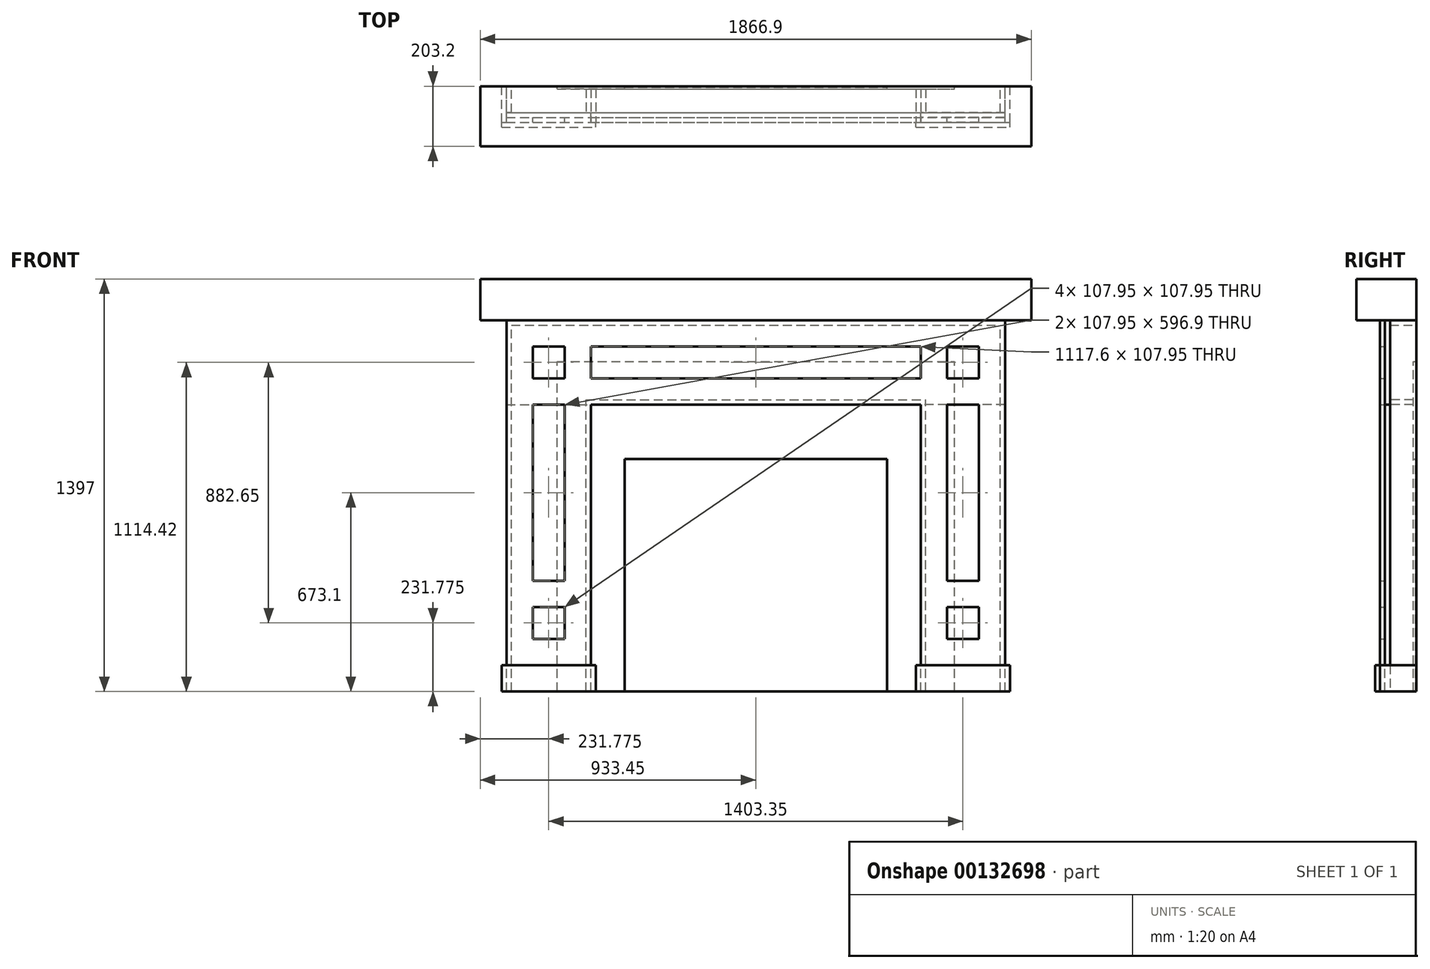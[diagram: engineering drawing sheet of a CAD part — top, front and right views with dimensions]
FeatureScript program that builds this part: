
annotation { "Feature Type Name" : "Feature", "Feature Type Description" : "" }
export const myFeature = defineFeature(function(context is Context, id is Id, definition is map)
    precondition{}
    {
        {
            var Q0;
            Q0=qCreatedBy(makeId("Front.planeOp"),FACE);
            var sketch = newSketch(context, id + "F0", { "sketchPlane" : qUnion([Q0])});
            skLineSegment(sketch, "E0.bottom", {"start": v(0, 0) * mm, "end": v(889, 0) * mm});
            skLineSegment(sketch, "E0.top", {"start": v(0, 787.4) * mm, "end": v(889, 787.4) * mm});
            skLineSegment(sketch, "E0.left", {"start": v(0, 0) * mm, "end": v(0, 787.4) * mm});
            skLineSegment(sketch, "E0.right", {"start": v(889, 0) * mm, "end": v(889, 787.4) * mm});
            skSolve(sketch);
        }
        {
            var Q0;
            Q0=makeQuery(id+"F0.imprint","IMPRINT",FACE,{"disambiguationData":[TD([[makeQuery(id+"F0.imprint","IMPRINT",EDGE,{"derivedFrom":sQuery(id+"F0.wireOp",EDGE,"E0.bottom")}),1.0]])]});
            extrude(context, id + "F1", {"entities" : qUnion([Q0]), "depth" : 2.54 * mm});
        }
        {
            var Q0;
            Q0=qCreatedBy(makeId("Front.planeOp"),FACE);
            var sketch = newSketch(context, id + "F2", { "sketchPlane" : qUnion([Q0])});
            skLineSegment(sketch, "E1.bottom", {"start": v(0, 0) * mm, "end": v(-228.6, 0) * mm});
            skLineSegment(sketch, "E1.left", {"start": v(0, 0) * mm, "end": v(0, 787.4) * mm});
            skLineSegment(sketch, "E2", {"start": v(0, 787.4) * mm, "end": v(889, 787.4) * mm});
            skLineSegment(sketch, "E3.0", {"start": v(889, 0) * mm, "end": v(889, 787.4) * mm});
            skLineSegment(sketch, "E4", {"start": v(889, 0) * mm, "end": v(1117.6, 0) * mm});
            skLineSegment(sketch, "E5", {"start": v(1117.6, 0) * mm, "end": v(1117.6, 1117.6) * mm});
            skLineSegment(sketch, "E6", {"start": v(-228.6, 0) * mm, "end": v(-228.6, 1117.6) * mm});
            skLineSegment(sketch, "E7", {"start": v(-228.6, 1117.6) * mm, "end": v(1117.6, 1117.6) * mm});
            skSolve(sketch);
        }
        {
            var Q0;
            Q0 = qSketchRegion(id + "F2", true);
            extrude(context, id + "F3", {"entities" : qUnion([Q0]), "operationType" : NewBodyOperationType.ADD, "depth" : 9.52 * mm});
        }
        {
            var Q0;
            Q0=qCreatedBy(makeId("Front.planeOp"),FACE);
            var sketch = newSketch(context, id + "F4", { "sketchPlane" : qUnion([Q0])});
            skLineSegment(sketch, "E8.bottom", {"start": v(1272.39, 0) * mm, "end": v(1289.05, 0) * mm});
            skLineSegment(sketch, "E8.top", {"start": v(1272.39, 1240.64) * mm, "end": v(1289.05, 1240.64) * mm});
            skLineSegment(sketch, "E8.left", {"start": v(1272.39, 0) * mm, "end": v(1272.39, 1240.64) * mm});
            skLineSegment(sketch, "E8.right", {"start": v(1289.05, 0) * mm, "end": v(1289.05, 1240.64) * mm});
            skLineSegment(sketch, "E9.bottom", {"start": v(-400.05, 1257.3) * mm, "end": v(1289.05, 1257.3) * mm});
            skLineSegment(sketch, "E9.top", {"start": v(-400.05, 1240.64) * mm, "end": v(1289.05, 1240.64) * mm});
            skLineSegment(sketch, "E9.left", {"start": v(-400.05, 1257.3) * mm, "end": v(-400.05, 1240.64) * mm});
            skLineSegment(sketch, "E9.right", {"start": v(1289.05, 1257.3) * mm, "end": v(1289.05, 1240.64) * mm});
            skLineSegment(sketch, "E10.bottom", {"start": v(-383.39, 0) * mm, "end": v(-400.05, 0) * mm});
            skLineSegment(sketch, "E10.top", {"start": v(-383.39, 1240.64) * mm, "end": v(-400.05, 1240.64) * mm});
            skLineSegment(sketch, "E10.left", {"start": v(-383.39, 0) * mm, "end": v(-383.39, 1240.64) * mm});
            skLineSegment(sketch, "E10.right", {"start": v(-400.05, 0) * mm, "end": v(-400.05, 1240.64) * mm});
            skSolve(sketch);
        }
        {
            var Q0;
            Q0=makeQuery(id+"F4.imprint","IMPRINT",FACE,{"disambiguationData":[TD([[makeQuery(id+"F4.imprint","IMPRINT",EDGE,{"derivedFrom":sQuery(id+"F4.wireOp",EDGE,"E10.bottom")}),-1.0]])]});
            var Q1;
            Q1=makeQuery(id+"F4.imprint","IMPRINT",FACE,{"disambiguationData":[TD([[makeQuery(id+"F4.imprint","IMPRINT",EDGE,{"derivedFrom":sQuery(id+"F4.wireOp",EDGE,"E9.bottom")}),-1.0]])]});
            var Q2;
            Q2=makeQuery(id+"F4.imprint","IMPRINT",FACE,{"disambiguationData":[TD([[makeQuery(id+"F4.imprint","IMPRINT",EDGE,{"derivedFrom":sQuery(id+"F4.wireOp",EDGE,"E8.bottom")}),1.0]])]});
            extrude(context, id + "F5", {"entities" : qUnion([Q0, Q1, Q2]), "depth" : 88.9 * mm});
        }
        {
            var Q0;
            Q0=makeQuery(id+"F5.opExtrude","CAP_FACE",FACE,{"disambiguationData":[OSD([sQuery(id+"F4.wireOp",EDGE,"E9.bottom"),sQuery(id+"F4.wireOp",EDGE,"E9.top"),sQuery(id+"F4.wireOp",EDGE,"E9.left"),sQuery(id+"F4.wireOp",EDGE,"E9.right")])],"isStart":false});
            var sketch = newSketch(context, id + "F6", { "sketchPlane" : qUnion([Q0])});
            skLineSegment(sketch, "E11.bottom", {"start": v(-400.05, 1257.3) * mm, "end": v(1289.05, 1257.3) * mm});
            skLineSegment(sketch, "E11.top", {"start": v(-400.05, 971.55) * mm, "end": v(1289.05, 971.55) * mm});
            skLineSegment(sketch, "E11.left", {"start": v(-400.05, 1257.3) * mm, "end": v(-400.05, 971.55) * mm});
            skLineSegment(sketch, "E11.right", {"start": v(1289.05, 1257.3) * mm, "end": v(1289.05, 971.55) * mm});
            skSolve(sketch);
        }
        {
            var Q0;
            Q0 = qSketchRegion(id + "F6", true);
            extrude(context, id + "F7", {"entities" : qUnion([Q0]), "depth" : 16.66 * mm});
        }
        {
            var Q0;
            Q0=makeQuery(id+"F5.opExtrude","CAP_FACE",FACE,{"disambiguationData":[OSD([sQuery(id+"F4.wireOp",EDGE,"E10.bottom"),sQuery(id+"F4.wireOp",EDGE,"E10.top"),sQuery(id+"F4.wireOp",EDGE,"E10.left"),sQuery(id+"F4.wireOp",EDGE,"E10.right")])],"isStart":false});
            var sketch = newSketch(context, id + "F8", { "sketchPlane" : qUnion([Q0])});
            skLineSegment(sketch, "E12.bottom", {"start": v(-400.05, 0) * mm, "end": v(-114.3, 0) * mm});
            skLineSegment(sketch, "E12.top", {"start": v(-400.05, 971.55) * mm, "end": v(-114.3, 971.55) * mm});
            skLineSegment(sketch, "E12.left", {"start": v(-400.05, 0) * mm, "end": v(-400.05, 971.55) * mm});
            skLineSegment(sketch, "E12.right", {"start": v(-114.3, 0) * mm, "end": v(-114.3, 971.55) * mm});
            skLineSegment(sketch, "E13.0", {"start": v(1289.05, 0) * mm, "end": v(1289.05, 971.55) * mm});
            skLineSegment(sketch, "E14.bottom", {"start": v(1289.05, 0) * mm, "end": v(1003.3, 0) * mm});
            skLineSegment(sketch, "E14.top", {"start": v(1289.05, 971.55) * mm, "end": v(1003.3, 971.55) * mm});
            skLineSegment(sketch, "E14.right", {"start": v(1003.3, 0) * mm, "end": v(1003.3, 971.55) * mm});
            skPoint(sketch, "E15.orphan", {"position": v(1289.05, 0) * mm});
            skSolve(sketch);
        }
        {
            var Q0;
            Q0 = qSketchRegion(id + "F8", true);
            extrude(context, id + "F9", {"entities" : qUnion([Q0]), "depth" : 16.66 * mm});
        }
        {
            var Q0;
            Q0=makeQuery(id+"F9.opExtrude","CAP_FACE",FACE,{"disambiguationData":[OSD([sQuery(id+"F8.wireOp",EDGE,"E12.bottom"),sQuery(id+"F8.wireOp",EDGE,"E12.top"),sQuery(id+"F8.wireOp",EDGE,"E12.left"),sQuery(id+"F8.wireOp",EDGE,"E12.right")])],"isStart":false});
            var sketch = newSketch(context, id + "F10", { "sketchPlane" : qUnion([Q0])});
            skLineSegment(sketch, "E16.0", {"start": v(-400.05, 0) * mm, "end": v(-400.05, 971.55) * mm});
            skLineSegment(sketch, "E17.0", {"start": v(-400.05, 1257.3) * mm, "end": v(-400.05, 971.55) * mm});
            skLineSegment(sketch, "E18.0", {"start": v(-400.05, 1257.3) * mm, "end": v(1289.05, 1257.3) * mm});
            skLineSegment(sketch, "E19.0", {"start": v(1289.05, 1257.3) * mm, "end": v(1289.05, 971.55) * mm});
            skLineSegment(sketch, "E20.0", {"start": v(1289.05, 0) * mm, "end": v(1289.05, 971.55) * mm});
            skLineSegment(sketch, "E21.0", {"start": v(1289.05, 0) * mm, "end": v(1003.3, 0) * mm});
            skLineSegment(sketch, "E22.0", {"start": v(1003.3, 0) * mm, "end": v(1003.3, 971.55) * mm});
            skLineSegment(sketch, "E23.0", {"start": v(-114.3, 971.55) * mm, "end": v(1003.3, 971.55) * mm});
            skLineSegment(sketch, "E24.0", {"start": v(-114.3, 0) * mm, "end": v(-114.3, 971.55) * mm});
            skLineSegment(sketch, "E25", {"start": v(-400.05, 0) * mm, "end": v(-114.3, 0) * mm});
            skLineSegment(sketch, "E26.bottom", {"start": v(-311.15, 177.8) * mm, "end": v(-203.2, 177.8) * mm});
            skLineSegment(sketch, "E26.top", {"start": v(-311.15, 285.75) * mm, "end": v(-203.2, 285.75) * mm});
            skLineSegment(sketch, "E26.left", {"start": v(-311.15, 177.8) * mm, "end": v(-311.15, 285.75) * mm});
            skLineSegment(sketch, "E26.right", {"start": v(-203.2, 177.8) * mm, "end": v(-203.2, 285.75) * mm});
            skLineSegment(sketch, "E27.bottom", {"start": v(-311.15, 1168.4) * mm, "end": v(-203.2, 1168.4) * mm});
            skLineSegment(sketch, "E27.top", {"start": v(-311.15, 1060.45) * mm, "end": v(-203.2, 1060.45) * mm});
            skLineSegment(sketch, "E27.left", {"start": v(-311.15, 1168.4) * mm, "end": v(-311.15, 1060.45) * mm});
            skLineSegment(sketch, "E27.right", {"start": v(-203.2, 1168.4) * mm, "end": v(-203.2, 1060.45) * mm});
            skPoint(sketch, "E28.oppositeSnap0", {"position": v(-203.2, 231.77) * mm});
            skLineSegment(sketch, "E28.bottom", {"start": v(-311.15, 374.65) * mm, "end": v(-203.2, 374.65) * mm});
            skLineSegment(sketch, "E28.top", {"start": v(-311.15, 971.55) * mm, "end": v(-203.2, 971.55) * mm});
            skLineSegment(sketch, "E28.left", {"start": v(-311.15, 374.65) * mm, "end": v(-311.15, 971.55) * mm});
            skLineSegment(sketch, "E28.right", {"start": v(-203.2, 374.65) * mm, "end": v(-203.2, 971.55) * mm});
            skLineSegment(sketch, "E29.bottom", {"start": v(-114.3, 1168.4) * mm, "end": v(1003.3, 1168.4) * mm});
            skLineSegment(sketch, "E29.top", {"start": v(-114.3, 1060.45) * mm, "end": v(1003.3, 1060.45) * mm});
            skLineSegment(sketch, "E29.left", {"start": v(-114.3, 1168.4) * mm, "end": v(-114.3, 1060.45) * mm});
            skLineSegment(sketch, "E29.right", {"start": v(1003.3, 1168.4) * mm, "end": v(1003.3, 1060.45) * mm});
            skLineSegment(sketch, "E30.bottom", {"start": v(1200.15, 1168.4) * mm, "end": v(1092.2, 1168.4) * mm});
            skLineSegment(sketch, "E30.top", {"start": v(1200.15, 1060.45) * mm, "end": v(1092.2, 1060.45) * mm});
            skLineSegment(sketch, "E30.left", {"start": v(1200.15, 1168.4) * mm, "end": v(1200.15, 1060.45) * mm});
            skLineSegment(sketch, "E30.right", {"start": v(1092.2, 1168.4) * mm, "end": v(1092.2, 1060.45) * mm});
            skLineSegment(sketch, "E31.bottom", {"start": v(1200.15, 177.8) * mm, "end": v(1092.2, 177.8) * mm});
            skLineSegment(sketch, "E31.top", {"start": v(1200.15, 285.75) * mm, "end": v(1092.2, 285.75) * mm});
            skLineSegment(sketch, "E31.left", {"start": v(1200.15, 177.8) * mm, "end": v(1200.15, 285.75) * mm});
            skLineSegment(sketch, "E31.right", {"start": v(1092.2, 177.8) * mm, "end": v(1092.2, 285.75) * mm});
            skLineSegment(sketch, "E32.bottom", {"start": v(1200.15, 374.65) * mm, "end": v(1092.2, 374.65) * mm});
            skLineSegment(sketch, "E32.top", {"start": v(1200.15, 971.55) * mm, "end": v(1092.2, 971.55) * mm});
            skLineSegment(sketch, "E32.left", {"start": v(1200.15, 374.65) * mm, "end": v(1200.15, 971.55) * mm});
            skLineSegment(sketch, "E32.right", {"start": v(1092.2, 374.65) * mm, "end": v(1092.2, 971.55) * mm});
            skSolve(sketch);
        }
        {
            var Q0;
            Q0 = qSketchRegion(id + "F10", true);
            extrude(context, id + "F11", {"entities" : qUnion([Q0]), "depth" : 16.66 * mm});
        }
        {
            var Q0;
            Q0=makeQuery(id+"F11.opExtrude","CAP_FACE",FACE,{"disambiguationData":[OSD([sQuery(id+"F10.wireOp",EDGE,"E16.0"),sQuery(id+"F10.wireOp",EDGE,"E17.0"),sQuery(id+"F10.wireOp",EDGE,"E18.0"),sQuery(id+"F10.wireOp",EDGE,"E19.0"),sQuery(id+"F10.wireOp",EDGE,"E20.0"),sQuery(id+"F10.wireOp",EDGE,"E21.0"),sQuery(id+"F10.wireOp",EDGE,"E22.0"),sQuery(id+"F10.wireOp",EDGE,"E23.0"),sQuery(id+"F10.wireOp",EDGE,"E24.0"),sQuery(id+"F10.wireOp",EDGE,"E25"),sQuery(id+"F10.wireOp",EDGE,"E26.bottom"),sQuery(id+"F10.wireOp",EDGE,"E26.top"),sQuery(id+"F10.wireOp",EDGE,"E26.left"),sQuery(id+"F10.wireOp",EDGE,"E26.right"),sQuery(id+"F10.wireOp",EDGE,"E27.bottom"),sQuery(id+"F10.wireOp",EDGE,"E27.top"),sQuery(id+"F10.wireOp",EDGE,"E27.left"),sQuery(id+"F10.wireOp",EDGE,"E27.right"),sQuery(id+"F10.wireOp",EDGE,"E28.bottom"),sQuery(id+"F10.wireOp",EDGE,"E28.top"),sQuery(id+"F10.wireOp",EDGE,"E28.left"),sQuery(id+"F10.wireOp",EDGE,"E28.right"),sQuery(id+"F10.wireOp",EDGE,"E29.bottom"),sQuery(id+"F10.wireOp",EDGE,"E29.top"),sQuery(id+"F10.wireOp",EDGE,"E29.left"),sQuery(id+"F10.wireOp",EDGE,"E29.right"),sQuery(id+"F10.wireOp",EDGE,"E30.bottom"),sQuery(id+"F10.wireOp",EDGE,"E30.top"),sQuery(id+"F10.wireOp",EDGE,"E30.left"),sQuery(id+"F10.wireOp",EDGE,"E30.right"),sQuery(id+"F10.wireOp",EDGE,"E31.bottom"),sQuery(id+"F10.wireOp",EDGE,"E31.top"),sQuery(id+"F10.wireOp",EDGE,"E31.left"),sQuery(id+"F10.wireOp",EDGE,"E31.right"),sQuery(id+"F10.wireOp",EDGE,"E32.bottom"),sQuery(id+"F10.wireOp",EDGE,"E32.top"),sQuery(id+"F10.wireOp",EDGE,"E32.left"),sQuery(id+"F10.wireOp",EDGE,"E32.right")])],"isStart":false});
            var sketch = newSketch(context, id + "F12", { "sketchPlane" : qUnion([Q0])});
            skLineSegment(sketch, "E33.bottom", {"start": v(-416.71, 88.9) * mm, "end": v(-97.64, 88.9) * mm});
            skLineSegment(sketch, "E33.top", {"start": v(-416.71, 0) * mm, "end": v(-97.64, 0) * mm});
            skLineSegment(sketch, "E33.left", {"start": v(-416.71, 88.9) * mm, "end": v(-416.71, 0) * mm});
            skLineSegment(sketch, "E33.right", {"start": v(-97.64, 88.9) * mm, "end": v(-97.64, 0) * mm});
            skLineSegment(sketch, "E34.bottom", {"start": v(986.64, 0) * mm, "end": v(1305.71, 0) * mm});
            skLineSegment(sketch, "E34.top", {"start": v(986.64, 88.9) * mm, "end": v(1305.71, 88.9) * mm});
            skLineSegment(sketch, "E34.left", {"start": v(986.64, 0) * mm, "end": v(986.64, 88.9) * mm});
            skLineSegment(sketch, "E34.right", {"start": v(1305.71, 0) * mm, "end": v(1305.71, 88.9) * mm});
            skSolve(sketch);
        }
        {
            var Q0;
            Q0 = qSketchRegion(id + "F12", true);
            extrude(context, id + "F13", {"entities" : qUnion([Q0]), "operationType" : NewBodyOperationType.ADD, "depth" : 16.66 * mm});
        }
        {
            var Q0;
            Q0=qCreatedBy(makeId("Front.planeOp"),FACE);
            var sketch = newSketch(context, id + "F14", { "sketchPlane" : qUnion([Q0])});
            skLineSegment(sketch, "E35.0", {"start": v(-400.05, 1257.3) * mm, "end": v(1289.05, 1257.3) * mm});
            skLineSegment(sketch, "E36.bottom", {"start": v(-488.95, 1257.3) * mm, "end": v(1377.95, 1257.3) * mm});
            skLineSegment(sketch, "E36.top", {"start": v(-488.95, 1397) * mm, "end": v(1377.95, 1397) * mm});
            skLineSegment(sketch, "E36.left", {"start": v(-488.95, 1257.3) * mm, "end": v(-488.95, 1397) * mm});
            skLineSegment(sketch, "E36.right", {"start": v(1377.95, 1257.3) * mm, "end": v(1377.95, 1397) * mm});
            skSolve(sketch);
        }
        {
            var Q0;
            Q0=makeQuery(id+"F14.imprint","IMPRINT",FACE,{"disambiguationData":[TD([[makeQuery(id+"F14.imprint","IMPRINT",EDGE,{"derivedFrom":sQuery(id+"F14.wireOp",EDGE,"E36.top")}),-1.0]])]});
            extrude(context, id + "F15", {"entities" : qUnion([Q0]), "depth" : 203.2 * mm});
        }
        {
            var Q0;
            Q0=makeQuery(id+"F11.opExtrude","SWEPT_FACE",FACE,{"disambiguationData":[OSD([sQuery(id+"F10.wireOp",EDGE,"E19.0"),sQuery(id+"F10.wireOp",EDGE,"E20.0")])]});
            var sketch = newSketch(context, id + "F16", { "sketchPlane" : qUnion([Q0])});
            skLineSegment(sketch, "E37.bottom", {"start": v(-122.22, 0) * mm, "end": v(0, 0) * mm});
            skLineSegment(sketch, "E37.top", {"start": v(-122.22, 88.9) * mm, "end": v(0, 88.9) * mm});
            skLineSegment(sketch, "E37.left", {"start": v(-122.22, 0) * mm, "end": v(-122.22, 88.9) * mm});
            skLineSegment(sketch, "E37.right", {"start": v(0, 0) * mm, "end": v(0, 88.9) * mm});
            skSolve(sketch);
        }
        {
            var Q0;
            Q0 = qSketchRegion(id + "F16", true);
            extrude(context, id + "F17", {"entities" : qUnion([Q0]), "depth" : 16.66 * mm});
        }
        {
            var Q0;
            Q0=makeQuery(id+"F11.opExtrude","SWEPT_FACE",FACE,{"disambiguationData":[OSD([sQuery(id+"F10.wireOp",EDGE,"E16.0"),sQuery(id+"F10.wireOp",EDGE,"E17.0")])]});
            var sketch = newSketch(context, id + "F18", { "sketchPlane" : qUnion([Q0])});
            skLineSegment(sketch, "E38.bottom", {"start": v(122.22, 0) * mm, "end": v(0, 0) * mm});
            skLineSegment(sketch, "E38.top", {"start": v(122.22, 88.9) * mm, "end": v(0, 88.9) * mm});
            skLineSegment(sketch, "E38.left", {"start": v(122.22, 0) * mm, "end": v(122.22, 88.9) * mm});
            skLineSegment(sketch, "E38.right", {"start": v(0, 0) * mm, "end": v(0, 88.9) * mm});
            skSolve(sketch);
        }
        {
            var Q0;
            {var subQ3=sQuery(id+"F18.wireOp",EDGE,"NJfkfWGk-EMKU-Osp6-6CeZ-PsvvD5t8buWZ.right");Q0=makeQuery(id+"F18.imprint","IMPRINT",FACE,{"disambiguationData":[TD([[makeQuery(id+"F18.imprint","IMPRINT",EDGE,{"derivedFrom":subQ3}),-1.0]])]});}
            var Q1;
            {var subQ3=sQuery(id+"F18.wireOp",EDGE,"E38.right");Q1=makeQuery(id+"F18.imprint","IMPRINT",FACE,{"disambiguationData":[TD([[makeQuery(id+"F18.imprint","IMPRINT",EDGE,{"derivedFrom":subQ3}),-1.0]])]});}
            var Q2;
            {var subQ5=sQuery(id+"F18.wireOp",EDGE,"E38.left");Q2=makeQuery(id+"F18.imprint","IMPRINT",FACE,{"disambiguationData":[TD([[makeQuery(id+"F18.imprint","IMPRINT",EDGE,{"derivedFrom":subQ5}),1.0]])]});}
            extrude(context, id + "F19", {"entities" : qUnion([Q0, Q1, Q2]), "depth" : 16.66 * mm});
        }
        {
            var Q0;
            Q0=makeQuery(id+"F9.opExtrude","CAP_FACE",FACE,{"disambiguationData":[OSD([sQuery(id+"F8.wireOp",EDGE,"E12.bottom"),sQuery(id+"F8.wireOp",EDGE,"E12.top"),sQuery(id+"F8.wireOp",EDGE,"E12.left"),sQuery(id+"F8.wireOp",EDGE,"E12.right")])],"isStart":true});
            var sketch = newSketch(context, id + "F20", { "sketchPlane" : qUnion([Q0])});
            skLineSegment(sketch, "E39.bottom", {"start": v(114.3, 0) * mm, "end": v(130.96, 0) * mm});
            skLineSegment(sketch, "E39.top", {"start": v(114.3, 971.55) * mm, "end": v(130.96, 971.55) * mm});
            skLineSegment(sketch, "E39.left", {"start": v(114.3, 0) * mm, "end": v(114.3, 971.55) * mm});
            skLineSegment(sketch, "E39.right", {"start": v(130.96, 0) * mm, "end": v(130.96, 971.55) * mm});
            skPoint(sketch, "E40.0", {"position": v(-1003.3, 0) * mm});
            skPoint(sketch, "E41.0", {"position": v(-1003.3, 971.55) * mm});
            skLineSegment(sketch, "E42.bottom", {"start": v(-1003.3, 0) * mm, "end": v(-1019.96, 0) * mm});
            skLineSegment(sketch, "E42.top", {"start": v(-1003.3, 971.55) * mm, "end": v(-1019.96, 971.55) * mm});
            skLineSegment(sketch, "E42.left", {"start": v(-1003.3, 0) * mm, "end": v(-1003.3, 971.55) * mm});
            skLineSegment(sketch, "E42.right", {"start": v(-1019.96, 0) * mm, "end": v(-1019.96, 971.55) * mm});
            skLineSegment(sketch, "E43.bottom", {"start": v(130.96, 971.55) * mm, "end": v(-1019.96, 971.55) * mm});
            skLineSegment(sketch, "E43.top", {"start": v(130.96, 988.21) * mm, "end": v(-1019.96, 988.21) * mm});
            skLineSegment(sketch, "E43.left", {"start": v(130.96, 971.55) * mm, "end": v(130.96, 988.21) * mm});
            skLineSegment(sketch, "E43.right", {"start": v(-1019.96, 971.55) * mm, "end": v(-1019.96, 988.21) * mm});
            skSolve(sketch);
        }
        {
            var Q0;
            Q0 = qSketchRegion(id + "F20", true);
            extrude(context, id + "F21", {"entities" : qUnion([Q0]), "depth" : 79.38 * mm});
        }
        {
            var Q0;
            Q0=makeQuery(id+"F21.opExtrude","SWEPT_FACE",FACE,{"disambiguationData":[OSD([sQuery(id+"F20.wireOp",EDGE,"E39.left")])]});
            var sketch = newSketch(context, id + "F22", { "sketchPlane" : qUnion([Q0])});
            skLineSegment(sketch, "E44.bottom", {"start": v(-9.53, 0) * mm, "end": v(-122.22, 0) * mm});
            skLineSegment(sketch, "E44.top", {"start": v(-9.53, 88.9) * mm, "end": v(-122.22, 88.9) * mm});
            skLineSegment(sketch, "E44.left", {"start": v(-9.53, 0) * mm, "end": v(-9.53, 88.9) * mm});
            skLineSegment(sketch, "E44.right", {"start": v(-122.22, 0) * mm, "end": v(-122.22, 88.9) * mm});
            skSolve(sketch);
        }
        {
            var Q0;
            Q0 = qSketchRegion(id + "F22", true);
            extrude(context, id + "F23", {"entities" : qUnion([Q0]), "depth" : 16.66 * mm});
        }
        {
            var Q0;
            Q0=makeQuery(id+"F21.opExtrude","SWEPT_FACE",FACE,{"disambiguationData":[OSD([sQuery(id+"F20.wireOp",EDGE,"E42.left")])]});
            var sketch = newSketch(context, id + "F24", { "sketchPlane" : qUnion([Q0])});
            skLineSegment(sketch, "E45.bottom", {"start": v(9.53, 0) * mm, "end": v(122.22, 0) * mm});
            skLineSegment(sketch, "E45.top", {"start": v(9.52, 88.9) * mm, "end": v(122.22, 88.9) * mm});
            skLineSegment(sketch, "E45.left", {"start": v(9.53, 0) * mm, "end": v(9.53, 88.9) * mm});
            skLineSegment(sketch, "E45.right", {"start": v(122.22, 0) * mm, "end": v(122.22, 88.9) * mm});
            skSolve(sketch);
        }
        {
            var Q0;
            {var subQ4=sQuery(id+"F24.wireOp",EDGE,"E45.left");Q0=makeQuery(id+"F24.imprint","IMPRINT",FACE,{"disambiguationData":[TD([[makeQuery(id+"F24.imprint","IMPRINT",EDGE,{"derivedFrom":subQ4}),-1.0]])]});}
            var Q1;
            {var subQ3=sQuery(id+"F24.wireOp",EDGE,"E45.right");Q1=makeQuery(id+"F24.imprint","IMPRINT",FACE,{"disambiguationData":[TD([[makeQuery(id+"F24.imprint","IMPRINT",EDGE,{"derivedFrom":subQ3}),1.0]])]});}
            extrude(context, id + "F25", {"entities" : qUnion([Q0, Q1]), "depth" : 16.66 * mm});
        }
    });
